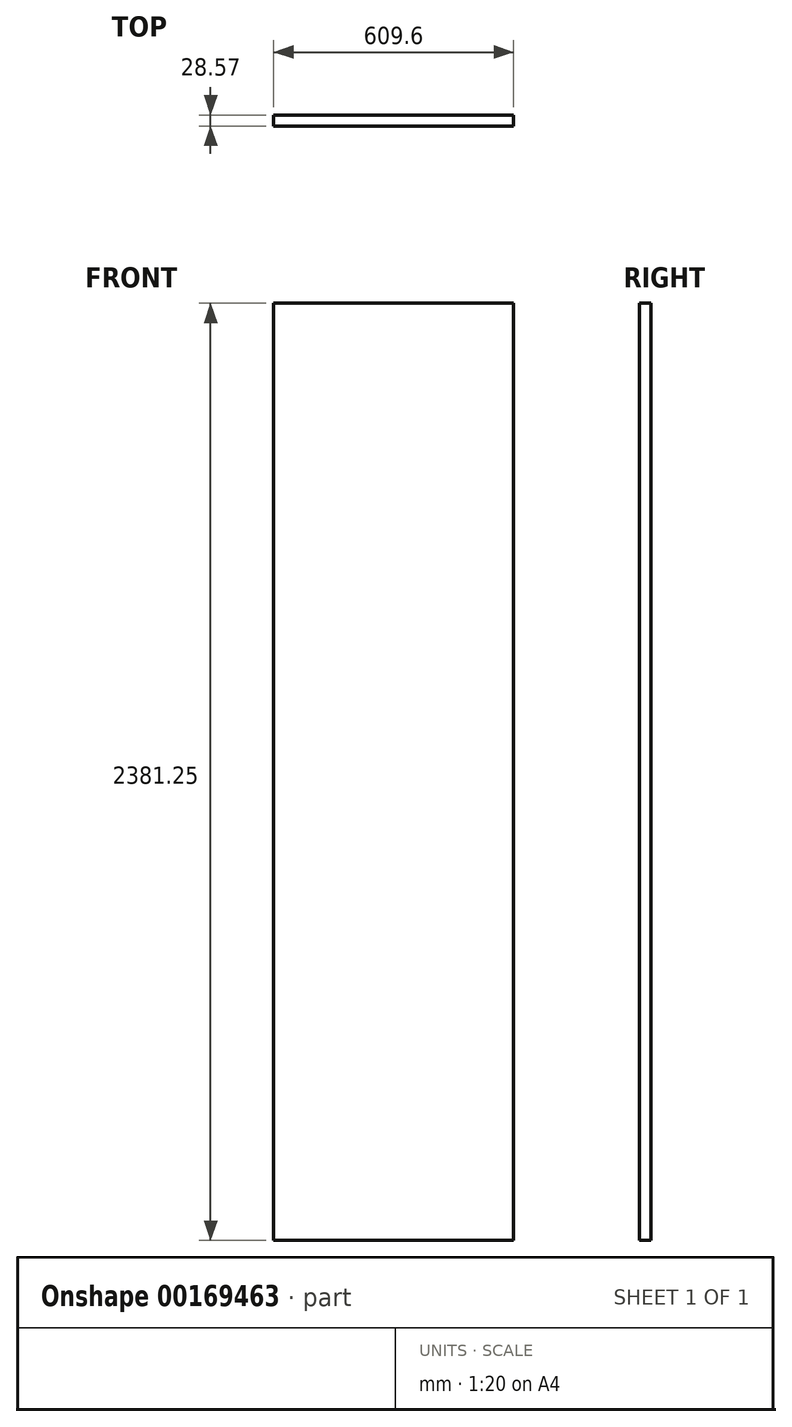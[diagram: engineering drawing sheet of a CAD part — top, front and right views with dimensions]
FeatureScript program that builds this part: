
annotation { "Feature Type Name" : "Feature", "Feature Type Description" : "" }
export const myFeature = defineFeature(function(context is Context, id is Id, definition is map)
    precondition{}
    {
        {
            var Q0;
            Q0=qCreatedBy(makeId("Front.planeOp"),FACE);
            var sketch = newSketch(context, id + "F0", { "sketchPlane" : qUnion([Q0])});
            skLineSegment(sketch, "E0.bottom", {"start": v(-301.25, 1775.26) * mm, "end": v(308.35, 1775.26) * mm});
            skLineSegment(sketch, "E0.top", {"start": v(-301.25, -606) * mm, "end": v(308.35, -606) * mm});
            skLineSegment(sketch, "E0.left", {"start": v(-301.25, 1775.26) * mm, "end": v(-301.25, -606) * mm});
            skLineSegment(sketch, "E0.right", {"start": v(308.35, 1775.26) * mm, "end": v(308.35, -606) * mm});
            skSolve(sketch);
        }
        {
            var Q0;
            Q0 = qSketchRegion(id + "F0", true);
            extrude(context, id + "F1", {"entities" : qUnion([Q0]), "depth" : 28.57 * mm});
        }
    });
